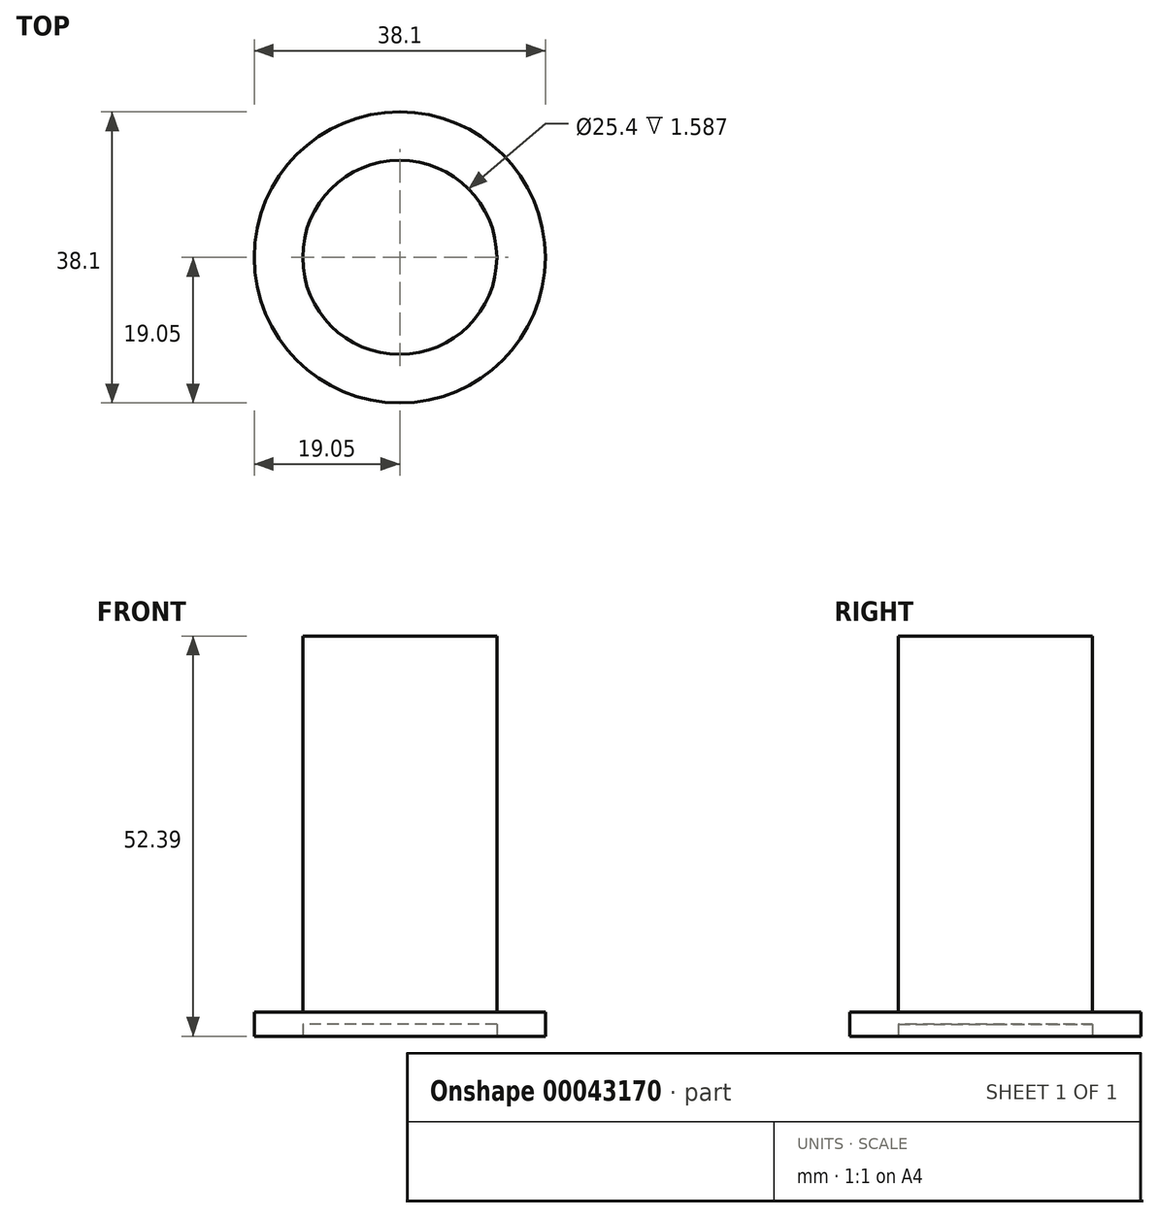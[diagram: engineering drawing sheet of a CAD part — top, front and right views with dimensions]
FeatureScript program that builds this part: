
annotation { "Feature Type Name" : "Feature", "Feature Type Description" : "" }
export const myFeature = defineFeature(function(context is Context, id is Id, definition is map)
    precondition{}
    {
        {
            var Q0;
            Q0=qCreatedBy(makeId("Top.planeOp"),FACE);
            var sketch = newSketch(context, id + "F0", { "sketchPlane" : qUnion([Q0])});
            skCircle(sketch, "E0", {"center": v(0, 0) * mm, "radius": 12.7 * mm});
            skCircle(sketch, "E1.0", {"center": v(0, 0) * mm, "radius": 19.05 * mm});
            skSolve(sketch);
        }
        {
            var Q0;
            Q0=makeQuery(id+"F0.imprint","IMPRINT",FACE,{"disambiguationData":[TD([[makeQuery(id+"F0.imprint","IMPRINT",EDGE,{"derivedFrom":sQuery(id+"F0.wireOp",EDGE,"E0")}),1.0]])]});
            extrude(context, id + "F1", {"entities" : qUnion([Q0]), "depth" : 50.8 * mm});
        }
        {
            var Q0;
            Q0=makeQuery(id+"F0.imprint","IMPRINT",FACE,{"disambiguationData":[TD([[makeQuery(id+"F0.imprint","IMPRINT",EDGE,{"derivedFrom":sQuery(id+"F0.wireOp",EDGE,"E0")}),-1.0]])]});
            extrude(context, id + "F2", {"entities" : qUnion([Q0]), "operationType" : NewBodyOperationType.ADD, "endBound" : BoundingType.SYMMETRIC, "depth" : 3.17 * mm});
        }
    });
